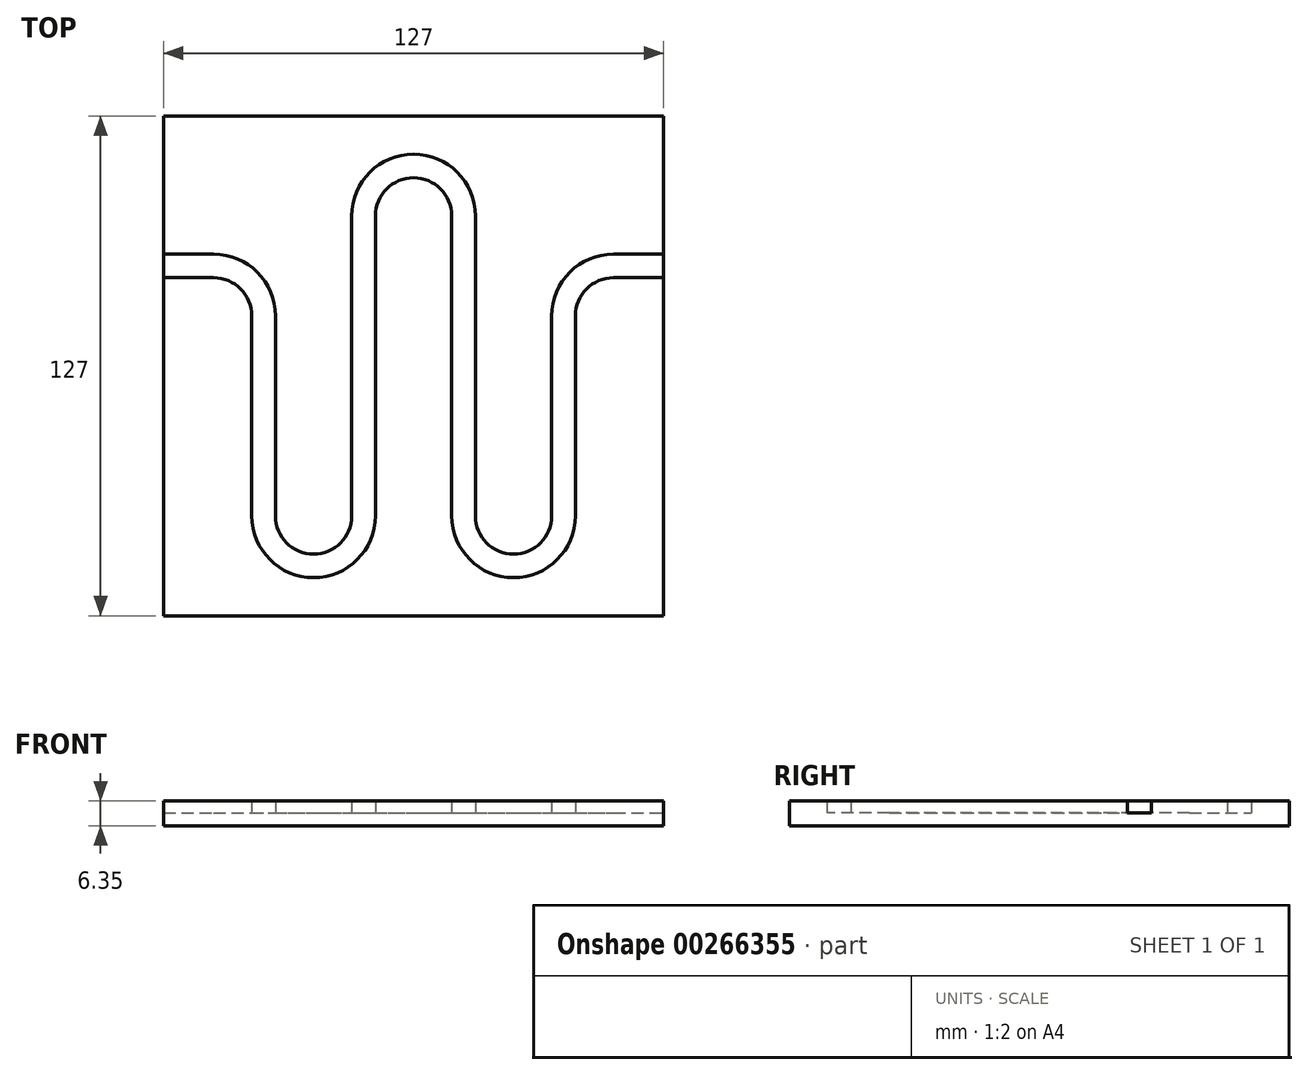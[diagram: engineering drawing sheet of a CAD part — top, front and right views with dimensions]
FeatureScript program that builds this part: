
annotation { "Feature Type Name" : "Feature", "Feature Type Description" : "" }
export const myFeature = defineFeature(function(context is Context, id is Id, definition is map)
    precondition{}
    {
        {
            var Q0;
            Q0=qCreatedBy(makeId("Front.planeOp"),FACE);
            var sketch = newSketch(context, id + "F0", { "sketchPlane" : qUnion([Q0])});
            skLineSegment(sketch, "E0.bottom", {"start": v(0, 0) * mm, "end": v(127, 0) * mm});
            skLineSegment(sketch, "E0.top", {"start": v(0, 6.35) * mm, "end": v(127, 6.35) * mm});
            skLineSegment(sketch, "E0.left", {"start": v(0, 0) * mm, "end": v(0, 6.35) * mm});
            skLineSegment(sketch, "E0.right", {"start": v(127, 0) * mm, "end": v(127, 6.35) * mm});
            skSolve(sketch);
        }
        {
            var Q0;
            Q0 = qSketchRegion(id + "F0", true);
            extrude(context, id + "F1", {"entities" : qUnion([Q0]), "oppositeDirection" : true, "depth" : 127 * mm});
        }
        {
            var Q0;
            Q0=makeQuery(id+"F1.opExtrude","SWEPT_FACE",FACE,{"disambiguationData":[OSD([sQuery(id+"F0.wireOp",EDGE,"E0.top")])]});
            var sketch = newSketch(context, id + "F2", { "sketchPlane" : qUnion([Q0])});
            skLineSegment(sketch, "E1", {"start": v(0, 88.9) * mm, "end": v(12.7, 88.9) * mm});
            skLineSegment(sketch, "E2", {"start": v(25.4, 76.2) * mm, "end": v(25.4, 25.4) * mm});
            skLineSegment(sketch, "E3", {"start": v(38.1, 12.7) * mm, "end": v(38.1, 12.7) * mm});
            skLineSegment(sketch, "E4", {"start": v(50.8, 25.4) * mm, "end": v(50.8, 76.2) * mm});
            skLineSegment(sketch, "E5", {"start": v(63.5, 88.9) * mm, "end": v(63.5, 88.9) * mm});
            skLineSegment(sketch, "E6", {"start": v(76.2, 76.2) * mm, "end": v(76.2, 25.4) * mm});
            skLineSegment(sketch, "E7", {"start": v(88.9, 12.7) * mm, "end": v(88.9, 12.7) * mm});
            skLineSegment(sketch, "E8", {"start": v(101.6, 25.4) * mm, "end": v(101.6, 76.2) * mm});
            skLineSegment(sketch, "E9", {"start": v(114.3, 88.9) * mm, "end": v(127, 88.9) * mm});
            skPoint(sketch, "E10.visualSharp", {"position": v(25.4, 88.9) * mm});
            skArc(sketch, "E10.filletArc", {"start": v(25.4, 76.2) * mm, "mid": v(21.68, 85.18) * mm, "end": v(12.7, 88.9) * mm});
            skPoint(sketch, "E11.visualSharp", {"position": v(25.4, 12.7) * mm});
            skArc(sketch, "E11.filletArc", {"start": v(25.4, 25.4) * mm, "mid": v(29.12, 16.42) * mm, "end": v(38.1, 12.7) * mm});
            skPoint(sketch, "E12.visualSharp", {"position": v(50.8, 12.7) * mm});
            skArc(sketch, "E12.filletArc", {"start": v(38.1, 12.7) * mm, "mid": v(47.08, 16.42) * mm, "end": v(50.8, 25.4) * mm});
            skPoint(sketch, "E13.visualSharp", {"position": v(50.8, 88.9) * mm});
            skPoint(sketch, "E14.visualSharp", {"position": v(76.2, 88.9) * mm});
            skPoint(sketch, "E15.visualSharp", {"position": v(76.2, 12.7) * mm});
            skArc(sketch, "E15.filletArc", {"start": v(76.2, 25.4) * mm, "mid": v(79.92, 16.42) * mm, "end": v(88.9, 12.7) * mm});
            skPoint(sketch, "E16.visualSharp", {"position": v(101.6, 12.7) * mm});
            skArc(sketch, "E16.filletArc", {"start": v(88.9, 12.7) * mm, "mid": v(97.88, 16.42) * mm, "end": v(101.6, 25.4) * mm});
            skPoint(sketch, "E17.visualSharp", {"position": v(101.6, 88.9) * mm});
            skArc(sketch, "E17.filletArc", {"start": v(114.3, 88.9) * mm, "mid": v(105.32, 85.18) * mm, "end": v(101.6, 76.2) * mm});
            skLineSegment(sketch, "E18", {"start": v(50.8, 76.2) * mm, "end": v(50.8, 101.6) * mm});
            skLineSegment(sketch, "E19", {"start": v(63.5, 114.3) * mm, "end": v(63.5, 114.3) * mm});
            skLineSegment(sketch, "E20", {"start": v(76.2, 101.6) * mm, "end": v(76.2, 76.2) * mm});
            skPoint(sketch, "E21.visualSharp", {"position": v(50.8, 114.3) * mm});
            skArc(sketch, "E21.filletArc", {"start": v(63.5, 114.3) * mm, "mid": v(54.52, 110.58) * mm, "end": v(50.8, 101.6) * mm});
            skPoint(sketch, "E22.visualSharp", {"position": v(76.2, 114.3) * mm});
            skArc(sketch, "E22.filletArc", {"start": v(76.2, 101.6) * mm, "mid": v(72.48, 110.58) * mm, "end": v(63.5, 114.3) * mm});
            skSolve(sketch);
        }
        {
            var Q0;
            Q0=makeQuery(id+"F1.opExtrude","SWEPT_FACE",FACE,{"disambiguationData":[OSD([sQuery(id+"F0.wireOp",EDGE,"E0.left")])]});
            var sketch = newSketch(context, id + "F3", { "sketchPlane" : qUnion([Q0])});
            skPoint(sketch, "E23.middle", {"position": v(-88.9, 6.35) * mm});
            skLineSegment(sketch, "E24.bottom", {"start": v(-85.9, 9.35) * mm, "end": v(-91.9, 9.35) * mm});
            skLineSegment(sketch, "E24.top", {"start": v(-85.9, 3.35) * mm, "end": v(-91.9, 3.35) * mm});
            skLineSegment(sketch, "E24.left", {"start": v(-85.9, 9.35) * mm, "end": v(-85.9, 3.35) * mm});
            skLineSegment(sketch, "E24.right", {"start": v(-91.9, 9.35) * mm, "end": v(-91.9, 3.35) * mm});
            skSolve(sketch);
        }
        {
            var Q0;
            {var subQ0=sQuery(id+"F3.wireOp",EDGE,"E24.top");Q0=makeQuery(id+"F3.imprint","IMPRINT",FACE,{"disambiguationData":[TD([[makeQuery(id+"F3.imprint","IMPRINT",EDGE,{"derivedFrom":subQ0}),-1.0]])]});}
            var Q1;
            Q1 = qConstructionFilter(qBodyType(qCreatedBy(id + "F2" ,EDGE), BodyType.WIRE), ConstructionObject.NO);
            sweep(context, id + "F4", {"operationType" : NewBodyOperationType.REMOVE, "profiles" : qUnion([Q0]), "path" : qUnion([Q1])});
        }
    });
